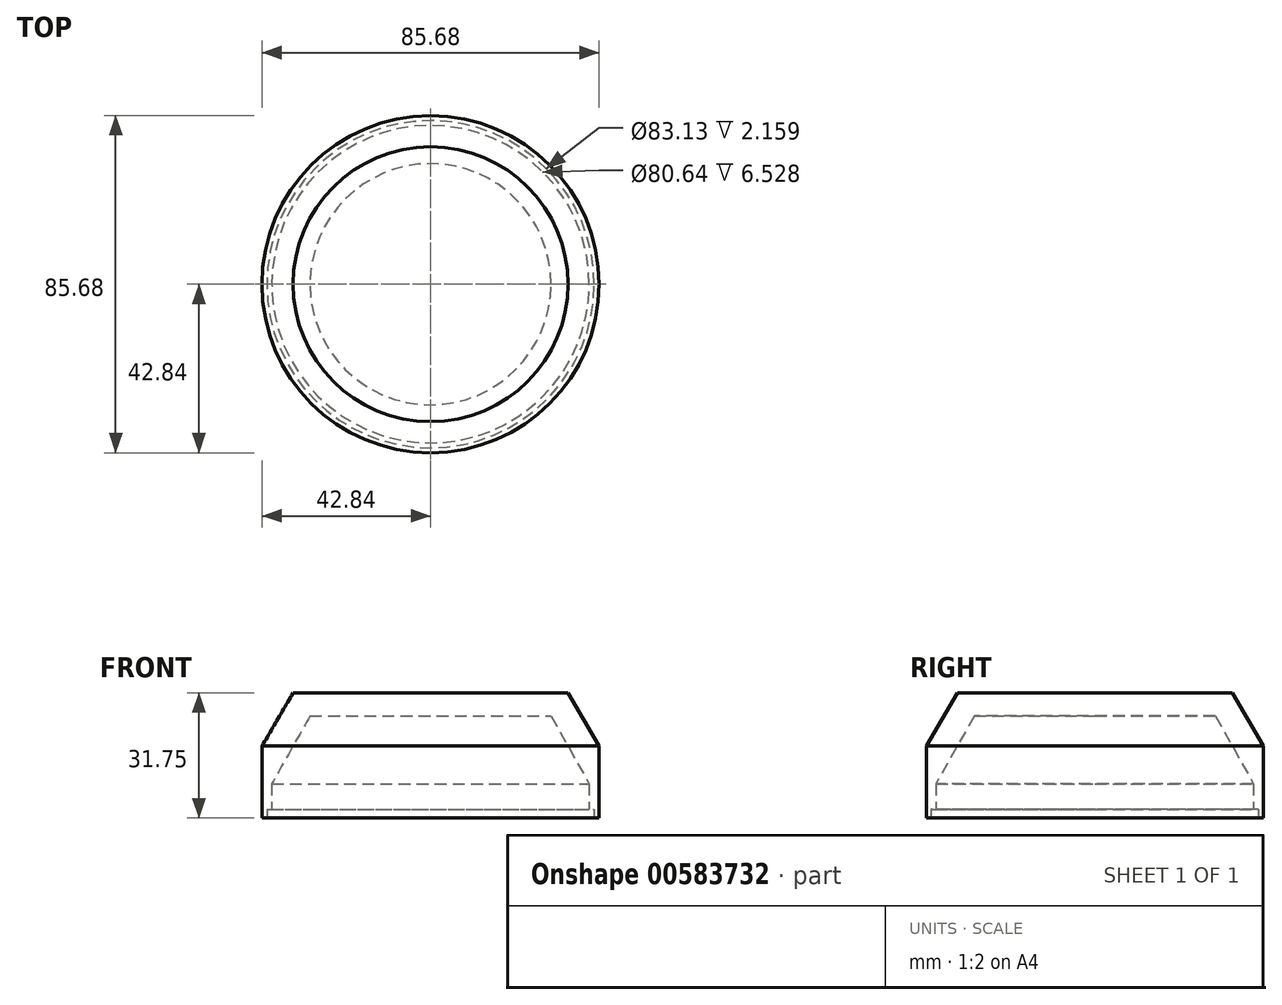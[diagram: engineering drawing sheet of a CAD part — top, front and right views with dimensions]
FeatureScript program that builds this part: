
annotation { "Feature Type Name" : "Feature", "Feature Type Description" : "" }
export const myFeature = defineFeature(function(context is Context, id is Id, definition is map)
    precondition{}
    {
        {
            var Q0;
            Q0=qCreatedBy(makeId("Front.planeOp"),FACE);
            var sketch = newSketch(context, id + "F0", { "sketchPlane" : qUnion([Q0])});
            skLineSegment(sketch, "E0", {"start": v(0, 0) * mm, "end": v(-34.92, 0) * mm});
            skLineSegment(sketch, "E1", {"start": v(-34.93, 0) * mm, "end": v(-42.84, -13.51) * mm});
            skLineSegment(sketch, "E2", {"start": v(-42.84, -13.51) * mm, "end": v(-42.84, -31.75) * mm});
            skLineSegment(sketch, "E3", {"start": v(-42.84, -31.75) * mm, "end": v(-41.57, -31.75) * mm});
            skLineSegment(sketch, "E4", {"start": v(-41.57, -31.75) * mm, "end": v(-41.57, -29.6) * mm});
            skLineSegment(sketch, "E5", {"start": v(-41.57, -29.6) * mm, "end": v(-40.32, -29.6) * mm});
            skLineSegment(sketch, "E6", {"start": v(-40.32, -29.6) * mm, "end": v(-40.32, -23.06) * mm});
            skLineSegment(sketch, "E7", {"start": v(-40.32, -23.06) * mm, "end": v(-30.63, -5.86) * mm});
            skLineSegment(sketch, "E8", {"start": v(-30.63, -5.86) * mm, "end": v(0, -5.86) * mm});
            skLineSegment(sketch, "E9", {"start": v(0, -5.86) * mm, "end": v(0, 0) * mm});
            skPoint(sketch, "E10.end.orphan", {"position": v(0, -11.53) * mm});
            skPoint(sketch, "E10.start.orphan", {"position": v(0, -23.06) * mm});
            skSolve(sketch);
        }
        {
            var Q0;
            Q0=makeQuery(id+"F0.imprint","IMPRINT",FACE,{"disambiguationData":[TD([[makeQuery(id+"F0.imprint","IMPRINT",EDGE,{"derivedFrom":sQuery(id+"F0.wireOp",EDGE,"E0")}),1.0]])]});
            var Q1;
            Q1=sQuery(id+"F0.wireOp",EDGE,"E9");
            revolve(context, id + "F1", {"entities" : qUnion([Q0]), "axis" : qUnion([Q1]), "revolveType" : RevolveType.FULL});
        }
    });
